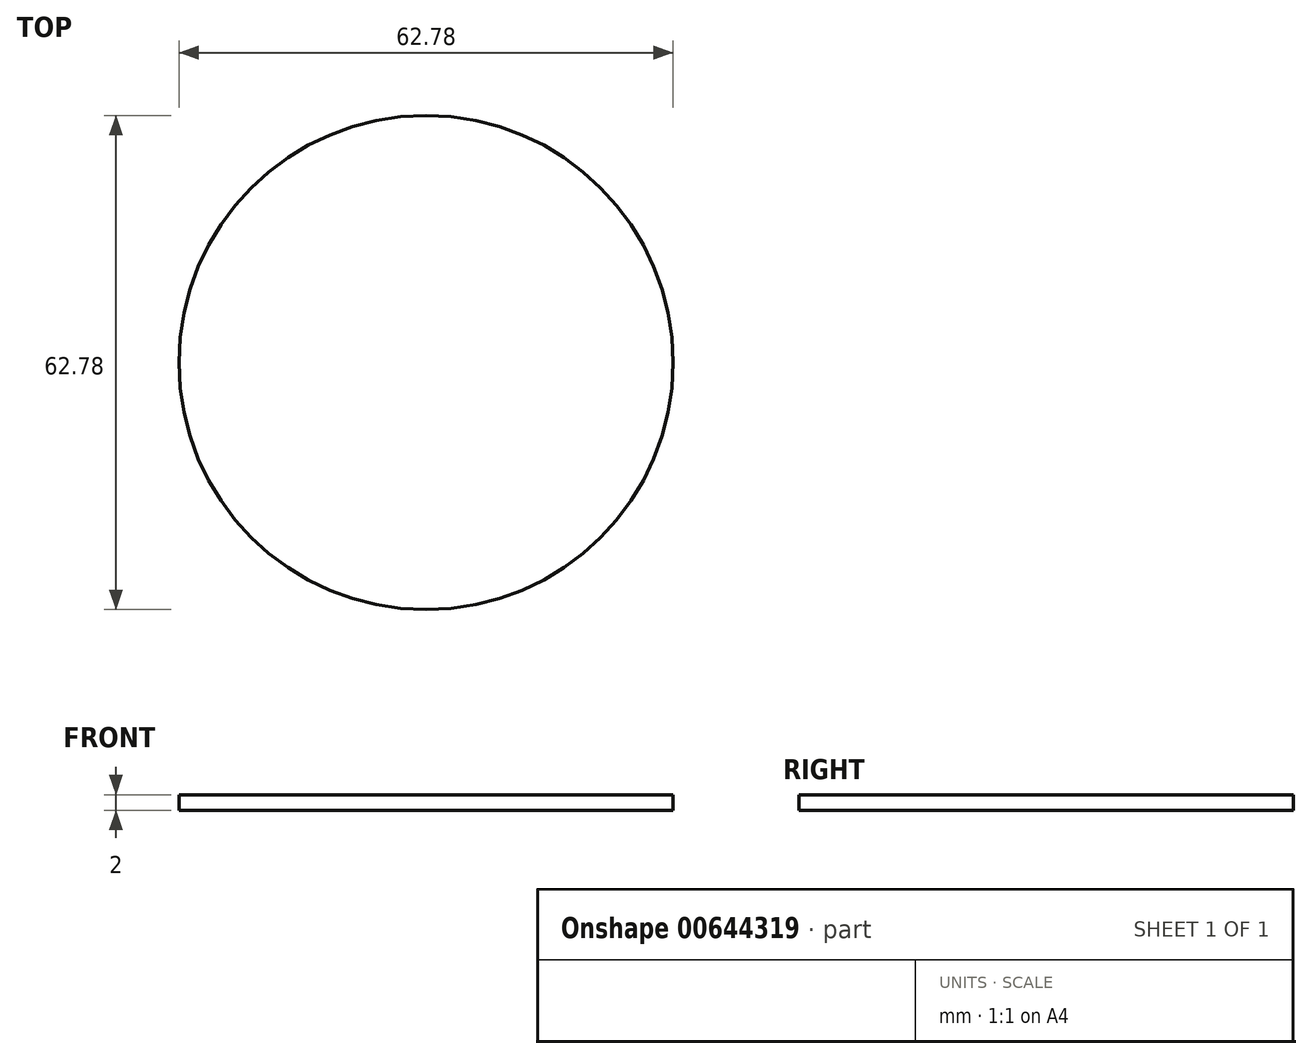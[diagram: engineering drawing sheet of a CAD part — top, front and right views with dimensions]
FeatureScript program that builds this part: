
annotation { "Feature Type Name" : "Feature", "Feature Type Description" : "" }
export const myFeature = defineFeature(function(context is Context, id is Id, definition is map)
    precondition{}
    {
        {
            var Q0;
            Q0=qCreatedBy(makeId("Top.planeOp"),FACE);
            var sketch = newSketch(context, id + "F0", { "sketchPlane" : qUnion([Q0])});
            skCircle(sketch, "E0", {"center": v(0, 0) * mm, "radius": 31.39 * mm});
            skSolve(sketch);
        }
        {
            var Q0;
            Q0=sQuery(id+"F0.wireOp",EDGE,"E0");
            extrude(context, id + "F1", {"bodyType" : ToolBodyType.SURFACE, "surfaceEntities" : qUnion([Q0]), "depth" : 2 * mm, "offsetDistance" : 25 * mm});
        }
    });
